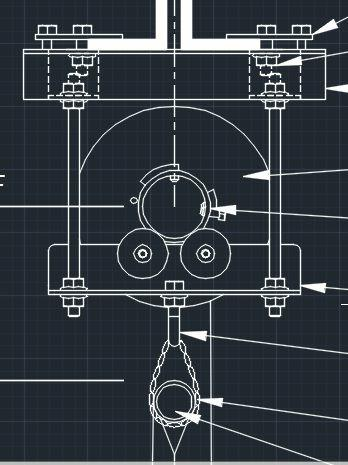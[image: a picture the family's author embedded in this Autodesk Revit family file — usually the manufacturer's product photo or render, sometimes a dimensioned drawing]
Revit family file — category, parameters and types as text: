
# Revit family: Gymnasium-Eqpt_Divider-Curtain_IPIbybison_FoldUp
name_source: partatom
category: Specialty Equipment
revit_build: Autodesk Revit 2018 (Build: 20170927_1515(x64)
units: mm (PartAtom-declared; Revit-internal decimal feet)

## family parameters
Always vertical = Yes
Cut with Voids When Loaded = No
OmniClass Number = 23.40.50.34.17
OmniClass Title = Gymnasium Dividers
Part Type = Normal
Room Calculation Point = No
Round Connector Dimension = Use Diameter
Shared = No

## types (1)
- as Specified
    Available Options = as Specified
    Description = IPI by Bison Motorized Fold Up Divider Curtain - IP850 as Specified
    Expected Lifespan (Years) = 0
    Keynote = 11 66 53
    Maintenance Schedule (Months) = 0
    Manufacturer = IPI by Bison
    Manufacturer Fax = 800-638-0698
    Manufacturer Website = https://ipibybison.com
    Maximum Size = 40' Height x 120' Length
    Model = IP850
    Product Data = http://www.arcat.com
    Revision = R1_2018-06
    Sales Information = https://ipibybison.com
    URL = https://ipibybison.com
    Warranty Duration (Years) = 0

## geometry (parser evidence)
native form markers: Sweep x6
no freeform markers — native parametric forms only
